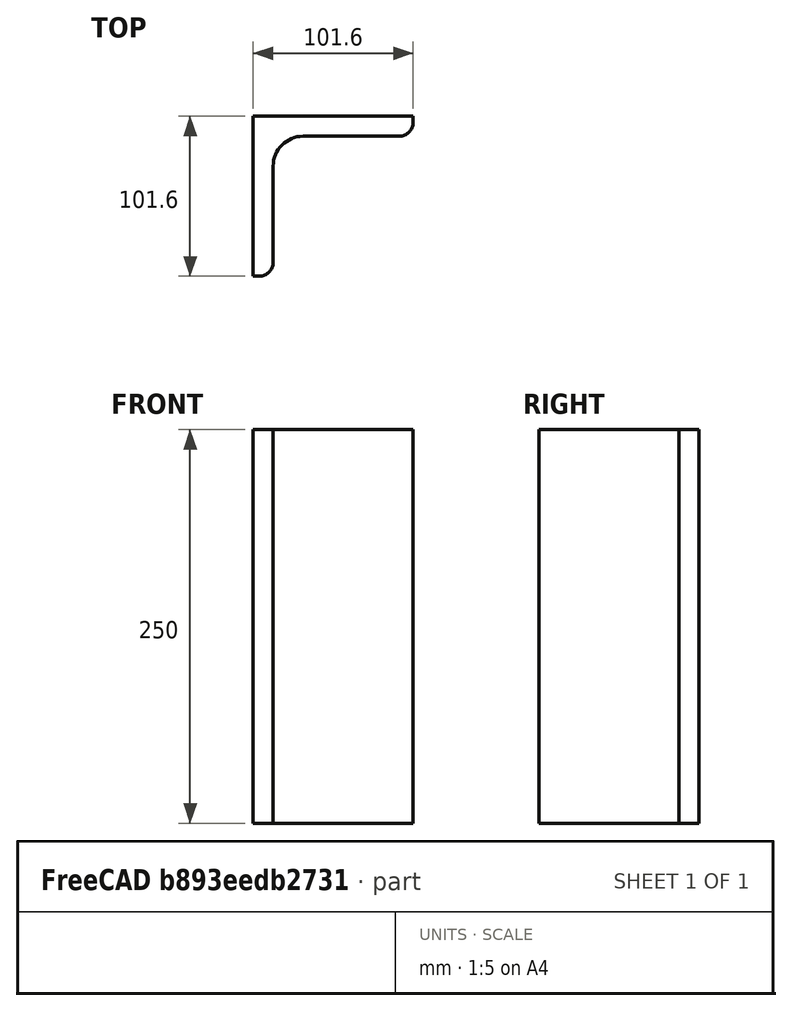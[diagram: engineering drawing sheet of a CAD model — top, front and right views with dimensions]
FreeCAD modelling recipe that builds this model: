
FCSTD DOCUMENT  (FreeCAD 0.19R16207 (Git))
Label: L BAR PLANILHA
License: CreativeCommons Attribution-NonCommercial-ShareAlike
LicenseURL: http://creativecommons.org/licenses/by-nc-sa/4.0/
objects: Sketcher::SketchObject×1, PartDesign::Pad×1, PartDesign::Body×1, Spreadsheet::Sheet×1
note: 4 computed .brp shape members not serialized (recipe doc carries the construction recipe); baked Part::Feature solids carry a one-line shape summary decoded from their .brp

FEATURE [Sketcher::SketchObject] Sketch
  MapMode = 5
  Support = -> [XY_Plane]
  expr: Constraints[21] = Spreadsheet.r1
  expr: Constraints[20] = Spreadsheet.r0
  expr: Constraints[19] = Spreadsheet.TKN
  expr: Constraints[18] = Spreadsheet.L
  sketch-geometry (9):
    g0: LineSegment StartX=0 StartY=0 StartZ=0 EndX=101.6 EndY=0 EndZ=0
    g1: LineSegment StartX=101.6 StartY=0 StartZ=0 EndX=101.6 EndY=-3.81 EndZ=0
    g2: ArcOfCircle CenterX=92.71 CenterY=-3.81 CenterZ=0 NormalX=0 NormalY=0 NormalZ=1 AngleXU=0 Radius=8.89 StartAngle=4.71239 EndAngle=6.28319
    g3: LineSegment StartX=92.71 StartY=-12.7 StartZ=0 EndX=31.75 EndY=-12.7 EndZ=0
    g4: ArcOfCircle CenterX=31.75 CenterY=-31.75 CenterZ=0 NormalX=0 NormalY=0 NormalZ=1 AngleXU=0 Radius=19.05 StartAngle=1.5708 EndAngle=3.14159
    g5: LineSegment StartX=12.7 StartY=-31.75 StartZ=0 EndX=12.7 EndY=-92.71 EndZ=0
    g6: ArcOfCircle CenterX=3.81 CenterY=-92.71 CenterZ=0 NormalX=0 NormalY=0 NormalZ=1 AngleXU=0 Radius=8.89 StartAngle=4.71239 EndAngle=6.28319
    g7: LineSegment StartX=3.81 StartY=-101.6 StartZ=0 EndX=0 EndY=-101.6 EndZ=0
    g8: LineSegment StartX=0 StartY=-101.6 StartZ=0 EndX=0 EndY=0 EndZ=0
  constraints (23):
    c: Horizontal(g0)
    c: Coincident(g0,g1)
    c: Vertical(g1)
    c: Tangent(g1,g2) = 1.5708
    c: Tangent(g2,g3) = 1.5708
    c: Tangent(g3,g4) = -1.5708
    c: Tangent(g4,g5) = -1.5708
    c: Tangent(g5,g6) = 1.5708
    c: Tangent(g6,g7) = 1.5708
    c: Coincident(g7,g8)
    c: Vertical(g8)
    c: Coincident(g0,g8)
    c: Coincident(g0,g-1)
    c: Vertical(g5)
    c: Horizontal(g7)
    c: Equal(g0,g8)
    c: Horizontal(g3)
    c: Equal(g6,g2)
    c: DistanceX(g0,g0) = 101.6
    c: DistanceX(g7,g5) = 12.7
    c: Radius(g2) = 8.89
    c: Radius(g4) = 19.05
    c: Equal(g7,g1)
FEATURE [PartDesign::Pad] Pad
  Length = 250
  Length2 = 100
  Profile = -> Sketch
  Type = 0
  expr: Length = Spreadsheet.H
FEATURE [PartDesign::Body] Body
  Group = -> [Sketch,Pad]
  Origin = -> Origin
  Tip = -> Pad
FEATURE [Spreadsheet::Sheet] Spreadsheet
  cells = A1=L - BAR; A2=L; B2(L)==4in; A3=TKN; B3(TKN)==0.5in; A4=H; B4(H)=250; A5=r0; B5(r0)==B3 * 0.7; A6=r1; B6(r1)==B3 * 1.5
